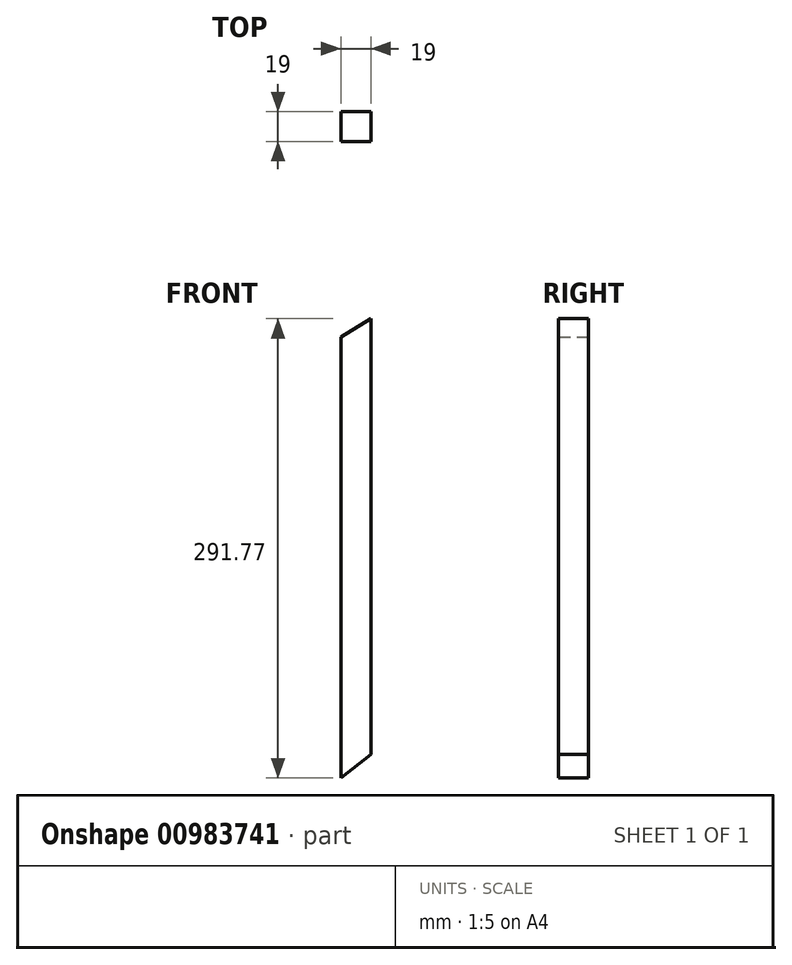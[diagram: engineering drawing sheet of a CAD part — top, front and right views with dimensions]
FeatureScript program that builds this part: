
annotation { "Feature Type Name" : "Feature", "Feature Type Description" : "" }
export const myFeature = defineFeature(function(context is Context, id is Id, definition is map)
    precondition{}
    {
        {
            var Q0;
            Q0=qCreatedBy(makeId("Front.planeOp"),FACE);
            var sketch = newSketch(context, id + "F0", { "sketchPlane" : qUnion([Q0])});
            skLineSegment(sketch, "E0.top", {"start": v(-12.52, -264.1) * mm, "end": v(6.48, -264.1) * mm});
            skLineSegment(sketch, "E0.left", {"start": v(-12.52, 15.9) * mm, "end": v(-12.52, -264.1) * mm});
            skLineSegment(sketch, "E0.right", {"start": v(6.48, 27.67) * mm, "end": v(6.48, -249.15) * mm});
            skLineSegment(sketch, "E1", {"start": v(6.48, 27.67) * mm, "end": v(-12.52, 15.9) * mm});
            skLineSegment(sketch, "E2", {"start": v(-12.52, -264.1) * mm, "end": v(6.48, -249.15) * mm});
            skSolve(sketch);
        }
        {
            var Q0;
            Q0 = qSketchRegion(id + "F0", true);
            extrude(context, id + "F1", {"entities" : qUnion([Q0]), "depth" : 19 * mm, "offsetDistance" : 25.4 * mm});
        }
    });
